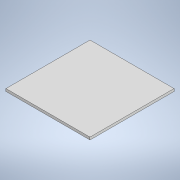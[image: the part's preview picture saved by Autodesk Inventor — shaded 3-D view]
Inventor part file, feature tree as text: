
AUTODESK INVENTOR PART (.ipt)
format: ipt  version: 2020.5 (Build 245400000, 400)  size: 90,624 bytes
history: native  units: mm
features: other x1, extrude x1, sketch x1
ambient origin geometry x8: Origin, YZ Plane, XZ Plane, XY Plane, X Axis, Y Axis, Z Axis, Center Point
bodies: Body1 (feature_tree)
feature tree (3):
  other  "Sólido1"
  extrude  "Extrusión1"  Depth=254.0mm
  sketch  "Boceto1"  dims[d0=254.0mm d1=254.0mm d2=7.62mm d3=0.0mm]
